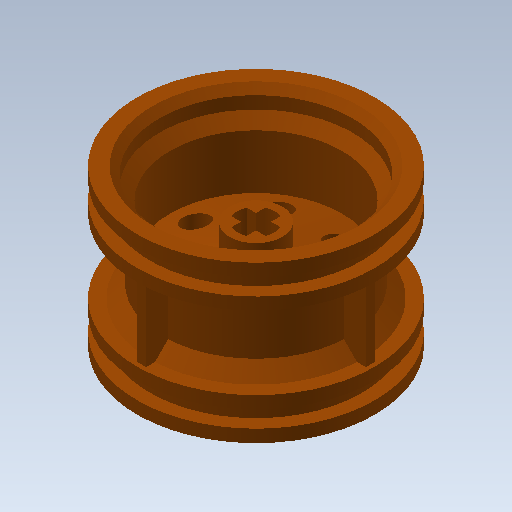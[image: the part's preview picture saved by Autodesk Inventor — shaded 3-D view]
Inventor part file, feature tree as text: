
AUTODESK INVENTOR PART (.ipt)
format: ipt  version: 2020 (Build 240168000, 168)  size: 413,696 bytes
history: native  units: mm
features: extrude x4, pattern_circular x2, other x1, revolve x1, plane x1
ambient origin geometry x8: Origin, YZ Plane, XZ Plane, XY Plane, X Axis, Y Axis, Z Axis, Center Point
bodies: Body1 (feature_tree)
feature tree (9):
  other  "Sólido1"
  revolve  "Revolution1"  Angle=90.0deg
  extrude  "Extrusion1"  Depth=4.0mm
  plane  "Work Plane1"
  extrude  "Extrusion2"  Depth=15.2mm
  extrude  "Extrusion3"  Depth=12.35mm
  pattern_circular  "Circular Pattern1"  [2 undecoded]
  extrude  "Extrusion4"  Depth=13.25mm
  pattern_circular  "Circular Pattern2"  Angle=45.0deg  [1 undecoded]
note: 3 required parameter values undecoded (feature->parameter linkage not recoverable at this tier; creation-order binding heuristic only, values carry confidence <= 0.55)
